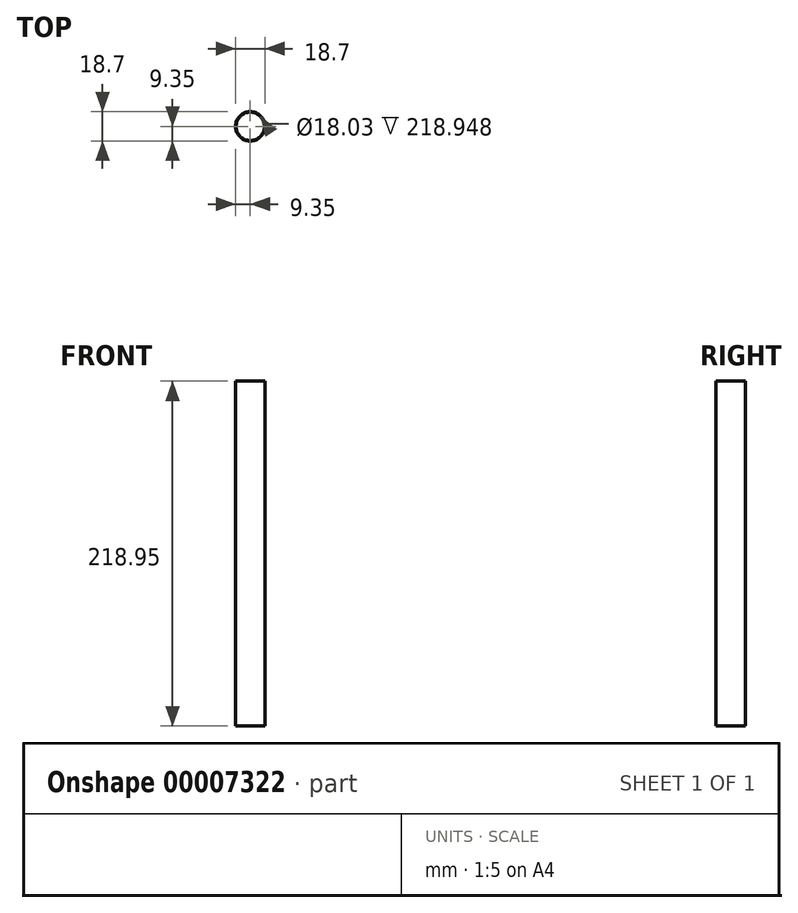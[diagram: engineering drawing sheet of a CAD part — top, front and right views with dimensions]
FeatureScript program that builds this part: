
annotation { "Feature Type Name" : "Feature", "Feature Type Description" : "" }
export const myFeature = defineFeature(function(context is Context, id is Id, definition is map)
    precondition{}
    {
        {
            var Q0;
            Q0=qCreatedBy(makeId("Front.planeOp"),FACE);
            var sketch = newSketch(context, id + "F0", { "sketchPlane" : qUnion([Q0])});
            skLineSegment(sketch, "E0.bottom", {"start": v(9.02, 0) * mm, "end": v(9.35, 0) * mm});
            skLineSegment(sketch, "E0.top", {"start": v(9.02, 218.95) * mm, "end": v(9.35, 218.95) * mm});
            skLineSegment(sketch, "E0.left", {"start": v(9.02, 0) * mm, "end": v(9.02, 218.95) * mm});
            skLineSegment(sketch, "E0.right", {"start": v(9.35, 0) * mm, "end": v(9.35, 218.95) * mm});
            skLineSegment(sketch, "E1", {"start": v(9.02, 0) * mm, "end": v(0, 0) * mm});
            skLineSegment(sketch, "E2", {"start": v(0, 0) * mm, "end": v(0, 218.95) * mm});
            skSolve(sketch);
        }
        {
            var Q0;
            Q0 = qSketchRegion(id + "F0", true);
            var Q1;
            Q1=sQuery(id+"F0.wireOp",EDGE,"E2");
            revolve(context, id + "F1", {"entities" : qUnion([Q0]), "axis" : qUnion([Q1]), "revolveType" : RevolveType.FULL});
        }
        {
            var Q0;
            Q0=qCreatedBy(makeId("Top.planeOp"),FACE);
            var sketch = newSketch(context, id + "F2", { "sketchPlane" : qUnion([Q0])});
            skCircle(sketch, "E3", {"center": v(0, 0) * mm, "radius": 63.5 * mm});
            skLineSegment(sketch, "E4", {"start": v(0, 0) * mm, "end": v(0, 63.5) * mm});
            skLineSegment(sketch, "E5", {"start": v(0, 0) * mm, "end": v(55, -31.75) * mm});
            skLineSegment(sketch, "E6.0", {"start": v(0.57, 0) * mm, "end": v(0.57, 63.5) * mm});
            skLineSegment(sketch, "E7.0.MirrorCS", {"start": v(-0.57, 0) * mm, "end": v(-0.57, 63.5) * mm});
            skLineSegment(sketch, "E8.0", {"start": v(-0.28, -0.49) * mm, "end": v(54.7, -32.24) * mm});
            skLineSegment(sketch, "E9", {"start": v(-0.57, 0) * mm, "end": v(0, 0) * mm});
            skLineSegment(sketch, "E10", {"start": v(0, 0) * mm, "end": v(0.57, 0) * mm});
            skLineSegment(sketch, "E11", {"start": v(0, 0) * mm, "end": v(-0.28, -0.49) * mm});
            skLineSegment(sketch, "E12.0.MirrorCS", {"start": v(0.28, 0.49) * mm, "end": v(55.27, -31.26) * mm});
            skLineSegment(sketch, "E13.0.MirrorCS", {"start": v(0, 0) * mm, "end": v(0.28, 0.49) * mm});
            skLineSegment(sketch, "E14.0.MirrorCS", {"start": v(0.28, -0.49) * mm, "end": v(-54.7, -32.24) * mm});
            skLineSegment(sketch, "E14.1.MirrorCS", {"start": v(0, 0) * mm, "end": v(-55, -31.75) * mm});
            skLineSegment(sketch, "E14.2.MirrorCS", {"start": v(-0.28, 0.49) * mm, "end": v(-55.27, -31.26) * mm});
            skLineSegment(sketch, "E15.0.MirrorCS", {"start": v(0, 0) * mm, "end": v(0.28, -0.49) * mm});
            skLineSegment(sketch, "E16.0.MirrorCS", {"start": v(0, 0) * mm, "end": v(-0.28, 0.49) * mm});
            skLineSegment(sketch, "E17.0.MirrorCS", {"start": v(0, 0) * mm, "end": v(0, -63.5) * mm});
            skCircle(sketch, "E18", {"center": v(0, -11.52) * mm, "radius": 2.17 * mm});
            skLineSegment(sketch, "E19", {"start": v(0, 0) * mm, "end": v(-2.17, 0) * mm});
            skLineSegment(sketch, "E20", {"start": v(-2.17, 0) * mm, "end": v(-2.17, -13.7) * mm});
            skLineSegment(sketch, "E21", {"start": v(-2.17, -13.7) * mm, "end": v(0, -13.7) * mm});
            skLineSegment(sketch, "E22.0.MirrorCS", {"start": v(0, 0) * mm, "end": v(2.17, 0) * mm});
            skLineSegment(sketch, "E23.0.MirrorCS", {"start": v(2.17, 0) * mm, "end": v(2.17, -13.7) * mm});
            skLineSegment(sketch, "E24.0.MirrorCS", {"start": v(2.17, -13.7) * mm, "end": v(0, -13.7) * mm});
            skCircle(sketch, "E25.0", {"center": v(0, 0) * mm, "radius": 9.35 * mm});
            skPoint(sketch, "E26", {"position": v(8.1, -4.67) * mm});
            skPoint(sketch, "E27", {"position": v(0, 9.35) * mm});
            skPoint(sketch, "E28", {"position": v(-8.1, -4.67) * mm});
            skPoint(sketch, "E29", {"position": v(0, -9.35) * mm});
            skSolve(sketch);
        }
        {
            var Q0;
            Q0=qCreatedBy(makeId("Top.planeOp"),FACE);
            var sketch = newSketch(context, id + "F3", { "sketchPlane" : qUnion([Q0])});
            skCircle(sketch, "E30.0", {"center": v(0, 0) * mm, "radius": 63.5 * mm});
            skLineSegment(sketch, "E31.0", {"start": v(0.57, 0) * mm, "end": v(0.57, 63.5) * mm});
            skLineSegment(sketch, "E32.0", {"start": v(0, 0) * mm, "end": v(0, 63.5) * mm});
            skLineSegment(sketch, "E33.0", {"start": v(0, 0) * mm, "end": v(0.57, 0) * mm});
            skLineSegment(sketch, "E34.0", {"start": v(-0.57, 0) * mm, "end": v(-0.57, 63.5) * mm});
            skLineSegment(sketch, "E35", {"start": v(0, 0) * mm, "end": v(63.5, 0) * mm});
            skCircle(sketch, "E36", {"center": v(0, 0) * mm, "radius": 0.57 * mm});
            skLineSegment(sketch, "E37.0.MirrorCS", {"start": v(0.57, 0) * mm, "end": v(0.57, -63.5) * mm});
            skLineSegment(sketch, "E38.0.MirrorCS", {"start": v(0, 0) * mm, "end": v(0, -63.5) * mm});
            skLineSegment(sketch, "E39.0.MirrorCS", {"start": v(-0.57, 0) * mm, "end": v(-0.57, -63.5) * mm});
            skLineSegment(sketch, "E40", {"start": v(0, 0.57) * mm, "end": v(63.5, 0.57) * mm});
            skLineSegment(sketch, "E41.0.MirrorCS", {"start": v(0, -0.57) * mm, "end": v(63.5, -0.57) * mm});
            skLineSegment(sketch, "E42.0.MirrorCS", {"start": v(0, 0.57) * mm, "end": v(-63.5, 0.57) * mm});
            skLineSegment(sketch, "E43.0.MirrorCS", {"start": v(0, 0) * mm, "end": v(-63.5, 0) * mm});
            skLineSegment(sketch, "E44.0.MirrorCS", {"start": v(0, -0.57) * mm, "end": v(-63.5, -0.57) * mm});
            skLineSegment(sketch, "E45", {"start": v(0, 0) * mm, "end": v(44.9, 44.9) * mm});
            skCircle(sketch, "E46", {"center": v(8.15, 8.15) * mm, "radius": 2.17 * mm});
            skCircle(sketch, "E47.0", {"center": v(0, 0) * mm, "radius": 9.35 * mm});
            skLineSegment(sketch, "E48", {"start": v(0, 0) * mm, "end": v(-1.54, 1.54) * mm});
            skLineSegment(sketch, "E49", {"start": v(-1.54, 1.54) * mm, "end": v(8.15, 11.22) * mm});
            skLineSegment(sketch, "E50", {"start": v(8.15, 11.22) * mm, "end": v(9.68, 9.68) * mm});
            skLineSegment(sketch, "E51.0.MirrorCS", {"start": v(11.22, 8.15) * mm, "end": v(9.68, 9.68) * mm});
            skLineSegment(sketch, "E52.0.MirrorCS", {"start": v(1.54, -1.54) * mm, "end": v(11.22, 8.15) * mm});
            skLineSegment(sketch, "E53.0.MirrorCS", {"start": v(0, 0) * mm, "end": v(1.54, -1.54) * mm});
            skPoint(sketch, "E54", {"position": v(9.35, 0) * mm});
            skPoint(sketch, "E55", {"position": v(-9.35, 0) * mm});
            skPoint(sketch, "E56", {"position": v(0, 9.35) * mm});
            skPoint(sketch, "E57", {"position": v(0, -9.35) * mm});
            skPoint(sketch, "E58", {"position": v(6.6, 6.6) * mm});
            skSolve(sketch);
        }
        {
            var Q0;
            Q0=qCreatedBy(makeId("Top.planeOp"),FACE);
            var sketch = newSketch(context, id + "F4", { "sketchPlane" : qUnion([Q0])});
            skCircle(sketch, "E59.0", {"center": v(0, 0) * mm, "radius": 63.5 * mm});
            skCircle(sketch, "E60.0", {"center": v(0, 0) * mm, "radius": 9.35 * mm});
            skLineSegment(sketch, "E61.0", {"start": v(0.57, 0) * mm, "end": v(0.57, 63.5) * mm});
            skLineSegment(sketch, "E62.0", {"start": v(0, 0) * mm, "end": v(0, 63.5) * mm});
            skLineSegment(sketch, "E63.0", {"start": v(-0.57, 0) * mm, "end": v(-0.57, 63.5) * mm});
            skLineSegment(sketch, "E64.0", {"start": v(0, 0) * mm, "end": v(0.57, 0) * mm});
            skLineSegment(sketch, "E65.0", {"start": v(0, 0) * mm, "end": v(0, -63.5) * mm});
            skLineSegment(sketch, "E66.0", {"start": v(2.17, 0) * mm, "end": v(2.17, -13.7) * mm});
            skLineSegment(sketch, "E67.0", {"start": v(-2.17, 0) * mm, "end": v(-2.17, -13.7) * mm});
            skLineSegment(sketch, "E68.0", {"start": v(0, 0) * mm, "end": v(-2.17, 0) * mm});
            skLineSegment(sketch, "E69.0", {"start": v(0, 0) * mm, "end": v(2.17, 0) * mm});
            skCircle(sketch, "E70.0", {"center": v(0, -11.52) * mm, "radius": 2.17 * mm});
            skLineSegment(sketch, "E71.0", {"start": v(-2.17, -13.7) * mm, "end": v(0, -13.7) * mm});
            skLineSegment(sketch, "E72.0", {"start": v(2.17, -13.7) * mm, "end": v(0, -13.7) * mm});
            skLineSegment(sketch, "E73", {"start": v(0, 0) * mm, "end": v(60.4, 19.62) * mm});
            skCircle(sketch, "E74", {"center": v(0, 0) * mm, "radius": 0.57 * mm});
            skLineSegment(sketch, "E75", {"start": v(0, 0) * mm, "end": v(37.32, -51.37) * mm});
            skLineSegment(sketch, "E76", {"start": v(-0.17, 0.54) * mm, "end": v(60.22, 20.16) * mm});
            skLineSegment(sketch, "E77", {"start": v(0, 0) * mm, "end": v(-0.17, 0.54) * mm});
            skLineSegment(sketch, "E78.0.MirrorCS", {"start": v(0.17, -0.54) * mm, "end": v(60.56, 19.08) * mm});
            skLineSegment(sketch, "E79.0.MirrorCS", {"start": v(0, 0) * mm, "end": v(0.17, -0.54) * mm});
            skLineSegment(sketch, "E80", {"start": v(0.46, 0.33) * mm, "end": v(37.78, -51.04) * mm});
            skLineSegment(sketch, "E81", {"start": v(0, 0) * mm, "end": v(0.46, 0.33) * mm});
            skLineSegment(sketch, "E82.0.MirrorCS", {"start": v(-0.46, -0.33) * mm, "end": v(36.87, -51.7) * mm});
            skLineSegment(sketch, "E83.0.MirrorCS", {"start": v(0, 0) * mm, "end": v(-0.46, -0.33) * mm});
            skLineSegment(sketch, "E84.0.MirrorCS", {"start": v(0.17, 0.54) * mm, "end": v(-60.22, 20.16) * mm});
            skLineSegment(sketch, "E85.0.MirrorCS", {"start": v(0, 0) * mm, "end": v(-60.4, 19.62) * mm});
            skLineSegment(sketch, "E86.0.MirrorCS", {"start": v(-0.17, -0.54) * mm, "end": v(-60.56, 19.08) * mm});
            skLineSegment(sketch, "E87.0.MirrorCS", {"start": v(0, 0) * mm, "end": v(0.17, 0.54) * mm});
            skLineSegment(sketch, "E88.0.MirrorCS", {"start": v(0, 0) * mm, "end": v(-0.17, -0.54) * mm});
            skLineSegment(sketch, "E89.0.MirrorCS", {"start": v(-0.46, 0.33) * mm, "end": v(-37.78, -51.04) * mm});
            skLineSegment(sketch, "E90.0.MirrorCS", {"start": v(0, 0) * mm, "end": v(-37.32, -51.37) * mm});
            skLineSegment(sketch, "E91.0.MirrorCS", {"start": v(0.46, -0.33) * mm, "end": v(-36.87, -51.7) * mm});
            skLineSegment(sketch, "E92.0.MirrorCS", {"start": v(0, 0) * mm, "end": v(0.46, -0.33) * mm});
            skLineSegment(sketch, "E93.0.MirrorCS", {"start": v(0, 0) * mm, "end": v(-0.46, 0.33) * mm});
            skPoint(sketch, "E94", {"position": v(0, 9.35) * mm});
            skPoint(sketch, "E95", {"position": v(8.89, 2.89) * mm});
            skPoint(sketch, "E96", {"position": v(5.5, -7.56) * mm});
            skPoint(sketch, "E97", {"position": v(-5.5, -7.56) * mm});
            skPoint(sketch, "E98", {"position": v(-8.89, 2.89) * mm});
            skSolve(sketch);
        }
        {
            var Q0;
            Q0=sQuery(id+"F2.wireOp",EDGE,"E5");
            var Q1;
            Q1=sQuery(id+"F2.wireOp",VERTEX,"E26");
            cPlane(context, id + "F5", {"entities" : qUnion([Q0, Q1]), "cplaneType" : CPlaneType.LINE_POINT, "offset" : 152.4 * mm, "width" : 152.4 * mm, "height" : 152.4 * mm});
        }
        {
            var Q0;
            Q0=sQuery(id+"F2.wireOp",EDGE,"E14.1.MirrorCS");
            var Q1;
            Q1=sQuery(id+"F2.wireOp",VERTEX,"E28");
            cPlane(context, id + "F6", {"entities" : qUnion([Q0, Q1]), "cplaneType" : CPlaneType.LINE_POINT, "offset" : 152.4 * mm, "width" : 152.4 * mm, "height" : 152.4 * mm});
        }
        {
            var Q0;
            Q0=sQuery(id+"F2.wireOp",EDGE,"E4");
            var Q1;
            Q1=sQuery(id+"F2.wireOp",VERTEX,"E27");
            cPlane(context, id + "F7", {"entities" : qUnion([Q0, Q1]), "cplaneType" : CPlaneType.LINE_POINT, "offset" : 152.4 * mm, "width" : 152.4 * mm, "height" : 152.4 * mm});
        }
        {
            var Q0;
            Q0=sQuery(id+"F2.wireOp",EDGE,"E17.0.MirrorCS");
            var Q1;
            Q1=sQuery(id+"F2.wireOp",VERTEX,"E29");
            cPlane(context, id + "F8", {"entities" : qUnion([Q0, Q1]), "cplaneType" : CPlaneType.LINE_POINT, "offset" : 152.4 * mm, "width" : 152.4 * mm, "height" : 152.4 * mm});
        }
        {
            var Q0;
            Q0=sQuery(id+"F3.wireOp",EDGE,"E45");
            var Q1;
            Q1=sQuery(id+"F3.wireOp",VERTEX,"E58");
            cPlane(context, id + "F9", {"entities" : qUnion([Q0, Q1]), "cplaneType" : CPlaneType.LINE_POINT, "offset" : 152.4 * mm, "width" : 152.4 * mm, "height" : 152.4 * mm});
        }
        {
            var Q0;
            Q0=sQuery(id+"F4.wireOp",EDGE,"E73");
            var Q1;
            Q1=sQuery(id+"F4.wireOp",VERTEX,"E95");
            cPlane(context, id + "F10", {"entities" : qUnion([Q0, Q1]), "cplaneType" : CPlaneType.LINE_POINT, "offset" : 152.4 * mm, "width" : 152.4 * mm, "height" : 152.4 * mm});
        }
        {
            var Q0;
            Q0=sQuery(id+"F4.wireOp",EDGE,"E75");
            var Q1;
            Q1=sQuery(id+"F4.wireOp",VERTEX,"E96");
            cPlane(context, id + "F11", {"entities" : qUnion([Q0, Q1]), "cplaneType" : CPlaneType.LINE_POINT, "offset" : 152.4 * mm, "width" : 152.4 * mm, "height" : 152.4 * mm});
        }
        {
            var Q0;
            Q0=sQuery(id+"F4.wireOp",EDGE,"E90.0.MirrorCS");
            var Q1;
            Q1=sQuery(id+"F4.wireOp",VERTEX,"E97");
            cPlane(context, id + "F12", {"entities" : qUnion([Q0, Q1]), "cplaneType" : CPlaneType.LINE_POINT, "offset" : 152.4 * mm, "width" : 152.4 * mm, "height" : 152.4 * mm});
        }
        {
            var Q0;
            Q0=sQuery(id+"F4.wireOp",EDGE,"E85.0.MirrorCS");
            var Q1;
            Q1=sQuery(id+"F4.wireOp",VERTEX,"E98");
            cPlane(context, id + "F13", {"entities" : qUnion([Q0, Q1]), "cplaneType" : CPlaneType.LINE_POINT, "offset" : 152.4 * mm, "width" : 152.4 * mm, "height" : 152.4 * mm});
        }
        {
            var Q0;
            Q0=qCreatedBy(makeId("Top.planeOp"),FACE);
            var sketch = newSketch(context, id + "F14", { "sketchPlane" : qUnion([Q0])});
            skLineSegment(sketch, "E99.0", {"start": v(0.28, -0.49) * mm, "end": v(-54.7, -32.24) * mm});
            skLineSegment(sketch, "E100.0", {"start": v(-0.28, 0.49) * mm, "end": v(-55.27, -31.26) * mm});
            skLineSegment(sketch, "E101.0", {"start": v(0, 0) * mm, "end": v(-55, -31.75) * mm});
            skCircle(sketch, "E102.0", {"center": v(0, 0) * mm, "radius": 9.35 * mm});
            skCircle(sketch, "E102.1", {"center": v(0, 0) * mm, "radius": 63.5 * mm});
            skLineSegment(sketch, "E103.0", {"start": v(0, 0) * mm, "end": v(-0.28, 0.49) * mm});
            skLineSegment(sketch, "E104.0", {"start": v(0, 0) * mm, "end": v(0.28, -0.49) * mm});
            skCircle(sketch, "E105", {"center": v(-8.32, -7.96) * mm, "radius": 2.17 * mm});
            skSolve(sketch);
        }
        {
            var Q0;
            Q0=sQuery(id+"F0.wireOp",VERTEX,"E2.end");
            var Q1;
            Q1=qCreatedBy(makeId("Origin.pointOp"),VERTEX);
            var Q2;
            Q2=sQuery(id+"F14.wireOp",VERTEX,"E105.center");
            cPlane(context, id + "F15", {"entities" : qUnion([Q0, Q1, Q2]), "cplaneType" : CPlaneType.THREE_POINT, "offset" : 152.4 * mm, "width" : 152.4 * mm, "height" : 152.4 * mm});
        }
    });
